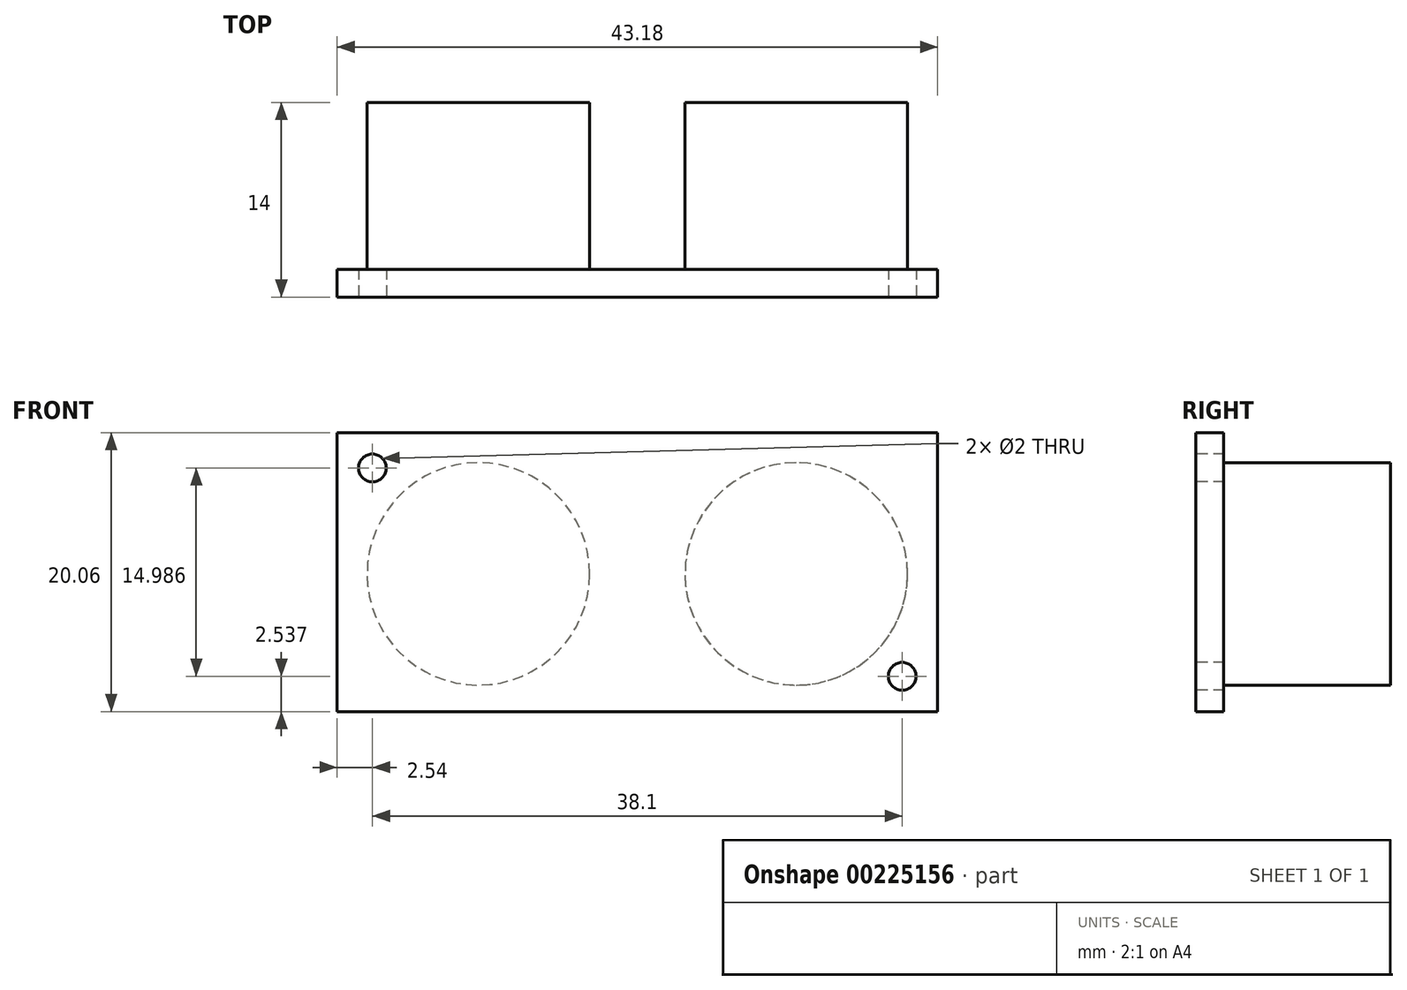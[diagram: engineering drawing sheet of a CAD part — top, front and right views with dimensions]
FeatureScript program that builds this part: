
annotation { "Feature Type Name" : "Feature", "Feature Type Description" : "" }
export const myFeature = defineFeature(function(context is Context, id is Id, definition is map)
    precondition{}
    {
        {
            var Q0;
            Q0=qCreatedBy(makeId("Front.planeOp"),FACE);
            var sketch = newSketch(context, id + "F0", { "sketchPlane" : qUnion([Q0])});
            skLineSegment(sketch, "E0.bottom", {"start": v(21.59, -10.03) * mm, "end": v(-21.59, -10.03) * mm});
            skLineSegment(sketch, "E0.top", {"start": v(21.59, 10.03) * mm, "end": v(-21.59, 10.03) * mm});
            skLineSegment(sketch, "E0.left", {"start": v(21.59, -10.03) * mm, "end": v(21.59, 10.03) * mm});
            skLineSegment(sketch, "E0.right", {"start": v(-21.59, -10.03) * mm, "end": v(-21.6, 10.03) * mm});
            skPoint(sketch, "E0.middle", {"position": v(0, 0) * mm});
            skSolve(sketch);
        }
        {
            var Q0;
            Q0 = qSketchRegion(id + "F0", true);
            extrude(context, id + "F1", {"entities" : qUnion([Q0]), "depth" : 2 * mm});
        }
        {
            var Q0;
            Q0=makeQuery(id+"F1.opExtrude","CAP_FACE",FACE,{"disambiguationData":[OSD([sQuery(id+"F0.wireOp",EDGE,"E0.bottom"),sQuery(id+"F0.wireOp",EDGE,"E0.top"),sQuery(id+"F0.wireOp",EDGE,"E0.left"),sQuery(id+"F0.wireOp",EDGE,"E0.right")])],"isStart":false});
            var sketch = newSketch(context, id + "F2", { "sketchPlane" : qUnion([Q0])});
            skLineSegment(sketch, "E1", {"start": v(-21.59, 0) * mm, "end": v(21.59, 0) * mm, "construction": true});
            skLineSegment(sketch, "E2", {"start": v(0, 10.03) * mm, "end": v(0, -10.03) * mm, "construction": true});
            skPoint(sketch, "E3", {"position": v(-19.05, 7.5) * mm});
            skPoint(sketch, "E4", {"position": v(19.05, -7.5) * mm});
            skSolve(sketch);
        }
        {
            var Q0;
            Q0=sQuery(id+"F2.wireOp",VERTEX,"E3");
            var Q1;
            Q1=sQuery(id+"F2.wireOp",VERTEX,"E4");
            var Q2;
            Q2=makeQuery(id+"F1.opExtrude","SWEPT_BODY",BODY,{"disambiguationData":[OSD([sQuery(id+"F0.wireOp",EDGE,"E0.bottom"),sQuery(id+"F0.wireOp",EDGE,"E0.top"),sQuery(id+"F0.wireOp",EDGE,"E0.left"),sQuery(id+"F0.wireOp",EDGE,"E0.right")])]});
            hole(context, id + "F3", {"style" : HoleStyle.SIMPLE, "endStyle" : HoleEndStyle.THROUGH, "holeDiameter" : 2 * mm, "locations" : qUnion([Q0, Q1]), "scope" : qUnion([Q2]), "isTappedThrough" : true});
        }
        {
            var Q0;
            Q0=makeQuery(id+"F1.opExtrude","CAP_FACE",FACE,{"disambiguationData":[OSD([sQuery(id+"F0.wireOp",EDGE,"E0.bottom"),sQuery(id+"F0.wireOp",EDGE,"E0.top"),sQuery(id+"F0.wireOp",EDGE,"E0.left"),sQuery(id+"F0.wireOp",EDGE,"E0.right")])],"isStart":true});
            var sketch = newSketch(context, id + "F4", { "sketchPlane" : qUnion([Q0])});
            skCircle(sketch, "E5", {"center": v(11.43, -0.13) * mm, "radius": 8 * mm});
            skLineSegment(sketch, "E6", {"start": v(0, 10.03) * mm, "end": v(0, -10.03) * mm, "construction": true});
            skCircle(sketch, "E7.MirrorC", {"center": v(-11.43, -0.13) * mm, "radius": 8 * mm});
            skSolve(sketch);
        }
        {
            var Q0;
            Q0 = qSketchRegion(id + "F4", true);
            extrude(context, id + "F5", {"entities" : qUnion([Q0]), "operationType" : NewBodyOperationType.ADD, "depth" : 12 * mm});
        }
    });
